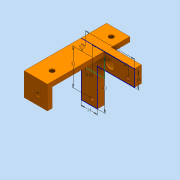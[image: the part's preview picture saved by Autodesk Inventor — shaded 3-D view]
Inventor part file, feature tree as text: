
AUTODESK INVENTOR PART (.ipt)
format: ipt  version: 2016 (Build 200138000, 138)  size: 231,424 bytes
history: native  units: mm
features: extrude x9, sketch x9, hole x7
ambient origin geometry x8: Origin, YZ Plane, XZ Plane, XY Plane, X Axis, Y Axis, Z Axis, Center Point
bodies: Solid1 (feature_tree)
feature tree (25):
  extrude  "Extrusion1"  Depth=20.0mm
  extrude  "Extrusion2"  Depth=45.0mm TaperAngle=0.0deg
  hole  "Hole2"  [1 undecoded]
  hole  "Hole3"  [1 undecoded]
  hole  "Hole4"  [1 undecoded]
  sketch  "Sketch3"  dims[d15=37.0mm d16=8.0mm d17=4.0mm d18=6.0mm d19=8.0mm d20=2.0mm d21=90.0deg d22=8.0mm d23=20.594885mm]
  sketch  "Sketch4"  dims[d24=37.0mm d25=8.0mm d26=4.0mm d27=6.0mm d28=8.0mm d29=2.0mm d30=90.0deg d31=8.0mm d32=20.594885mm]
  sketch  "Sketch5"  dims[d33=8.0mm d34=8.0mm d35=4.0mm d36=6.0mm d37=8.0mm d38=2.0mm d39=90.0deg d40=8.0mm d41=20.594885mm d51=7.0mm]
  extrude  "Extrusion3"  Depth=14.0mm
  extrude  "Extrusion4"  Depth=42.0mm
  extrude  "Extrusion5"  Depth=5.5mm
  sketch  "Sketch6"  dims[d52=7.0mm d53=7.0mm]
  extrude  "Extrusion6"  Depth=5.5mm
  hole  "Hole5"  [1 undecoded]
  extrude  "Extrusion7"  Depth=2.0mm
  hole  "Hole6"  [1 undecoded]
  hole  "Hole7"  [1 undecoded]
  sketch  "Sketch8"  dims[d58=3.2mm d59=0.0mm d62=14.0mm]
  extrude  "Extrusion8"  Depth=20.0mm
  extrude  "Extrusion9"  Depth=4.0mm
  hole  "Hole8"  [1 undecoded]
  sketch  "Sketch1"  dims[d0=20.0mm d1=20.0mm]
  sketch  "Sketch2"  dims[d2=4.0mm d3=0.0mm d4=45.0mm d5=0.0mm]
  sketch  "Sketch7"  dims[d54=3.2mm d55=0.0mm d56=3.2mm d57=0.0mm]
  sketch  "Sketch9"  dims[d65=42.0mm d66=42.0mm d68=5.5mm d69=5.5mm d70=31.0mm d71=31.0mm d72=14.0mm d73=6.0mm d74=0.0mm d75=3.0mm d76=6.0mm d77=4.0mm d78=2.0mm d79=90.0deg d80=8.0mm d81=20.594885mm d82=20.0mm d83=4.0mm d84=4.0mm d85=20.0mm d86=16.0mm d87=0.0mm d88=8.0mm d89=8.0mm d90=4.0mm d91=6.0mm d92=4.0mm d93=2.0mm d94=90.0deg d95=8.0mm d96=20.594885mm d97=8.0mm d98=8.0mm d99=4.0mm d100=6.0mm d101=4.0mm d102=2.0mm d103=90.0deg d104=8.0mm d105=20.594885mm d106=7.0mm d107=7.0mm d108=3.2mm d109=0.0mm d110=3.2mm d111=0.0mm d112=25.0mm d113=7.0mm d114=8.0mm d115=6.0mm d116=4.0mm d117=2.0mm d118=90.0deg d119=8.0mm d120=20.594885mm]
note: 7 required parameter values undecoded (feature->parameter linkage not recoverable at this tier; creation-order binding heuristic only, values carry confidence <= 0.55)
